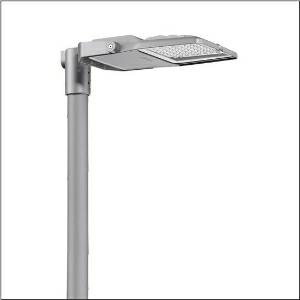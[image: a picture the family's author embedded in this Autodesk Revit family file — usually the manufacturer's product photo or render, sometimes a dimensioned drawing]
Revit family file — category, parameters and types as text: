
# Revit family: floodlight_fl_21_mini___pl52_5xa7776c2d3a_1d2c
name_source: partatom
category: Lighting Fixtures
units: mm (PartAtom-declared; Revit-internal decimal feet)

## family parameters
Cut with Voids When Loaded = No
Host = Face
Light Source = No
Part Type = Normal
Room Calculation Point = No
Round Connector Dimension = Use Diameter
Shared = No

## types (1)
- --- (1 x LED, 12190 lm, 89 W, 3000K)
    Apparent Load = 89 VA
    CIE Flux Codes = 26 60 98 100 100
    Color Rendering = 70
    Color Temperature = 3000K
    Default Elevation = 1800 mm
    Description = Floodlight FL 21 mini, floodlight, primary light control with lens, of PMMA, primary optical cover: protective disc, of toughened safety glass, transparent, light distribution: PL52, light emission: direct distribution, installation type: surface-mounted, LED, High Power LED, rated luminous flux: 12.190lm, luminous efficacy: 137lm/W, light colour: 730, colour temperature: 3000K, control gear: Smart Interface (Zhaga), control: flexible luminous flux parameterisation, time-dependent luminous flux control, constant luminous flux control, overheat protection, pre-setting: logarithmic dimming characteristic, with terminal, 6-pole, mains connection: 220..240V, AC, 50/60Hz, start of lifetime: 89W, end of service life: 94W, reduction: 43W, luminaire housing, of diecast aluminium, powder-coated, Siteco® metallic grey (DB 702S), corrosivity category C5 mid according to DIN EN ISO 12944, suitable for swimming pools, chlorine-resistant, sealing non-destructively replaceable, please order mast flange separately, mast bracket, of steel, galvanised, powder-coated, Siteco® metallic grey (DB 702S), Smart Interface below and above, protection rating (complete): IP66, insulation class (complete): insulation class II (safety insulation), certification: CE, ENEC, VDE, protection symbol: D, impact resistance: IK08, permissible operating ambient temperature: -40..+40°C, permissible operating ambient temperature for outdoor applications: -40..+50°C, standard: DIN EN 12944, LABS conformity tested according to VDMA 24364:2018-05, packaging unit: 1 piece

Light Distribution: PL52
    Height = 70 mm
    Lamp = 1 x LED
    Lamp Light Flux = 12190 lm
    Lamp Power = 89 W
    Lamp count = 1
    Length = 485 mm
    Luminous efficacy = 137 lm/W
    Manufacturer = Siteco
    ModVariant = No
    Model = 5XA7776C2D3A
    Number of Poles = 1
    OnlyDefault = Yes
    Power Factor = 1
    Product Name = Floodlight FL 21 mini | PL52
    Product group = floodlight | pylon annexe
    ProductGroupID = 6201
    Protection Class = Protection class II
    Protection Degree = IP 66
    RLX_Detail_Level = 1
    RLX_Emergency_Light_Flux = 0 lm
    RLX_Emergency_Type = 0
    RLX_Emergency_Type_DB = No
    RlxData = <blob elided: 101181 chars, md5=0eaa1946>
    Socket = socket
    Standby Power = 0 W
    System Light Flux = 12190 lm
    System Power = 89 W
    Type Comments = factory setting: luminous flux: 100 % | dim-lin: 254 | 456 mA
    Type Image = l_1007125.jpg
    URL = http://relux.com
    VarID = @adj_184707
    Voltage = 0 V
    Weight = 0.00 kg
    Width = 337 mm

## geometry (parser evidence)
native form markers: Blend x4, Sweep x14
no freeform markers — native parametric forms only
